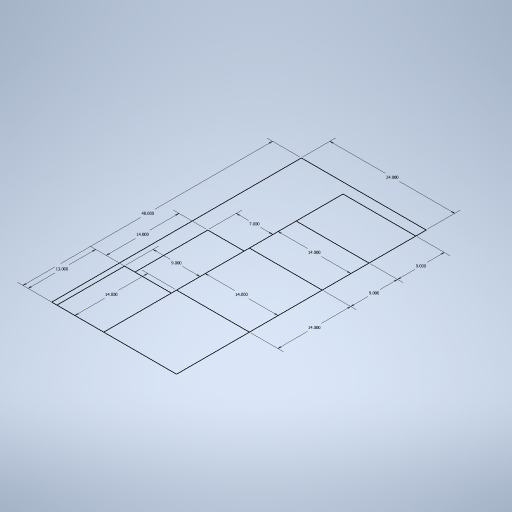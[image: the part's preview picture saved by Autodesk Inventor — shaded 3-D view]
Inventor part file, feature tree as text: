
AUTODESK INVENTOR PART (.ipt)
format: ipt  version: 2024 (Build 280153000, 153)  size: 250,368 bytes
history: native  units: in
note: dims shown in document units (in); Inventor stores cm internally (conversion verified against a paired STEP export)
features: sketch x1
ambient origin geometry x8: Origin, YZ Plane, XZ Plane, XY Plane, X Axis, Y Axis, Z Axis, Center Point
feature tree (1):
  sketch  "Sketch1"  dims[d0=24.0in d1=48.0in d2=14.0in d3=14.0in d4=14.0in d5=14.0in d6=9.0in d7=9.0in d8=9.0in d9=13.0in d10=7.0in d11=14.0in]
